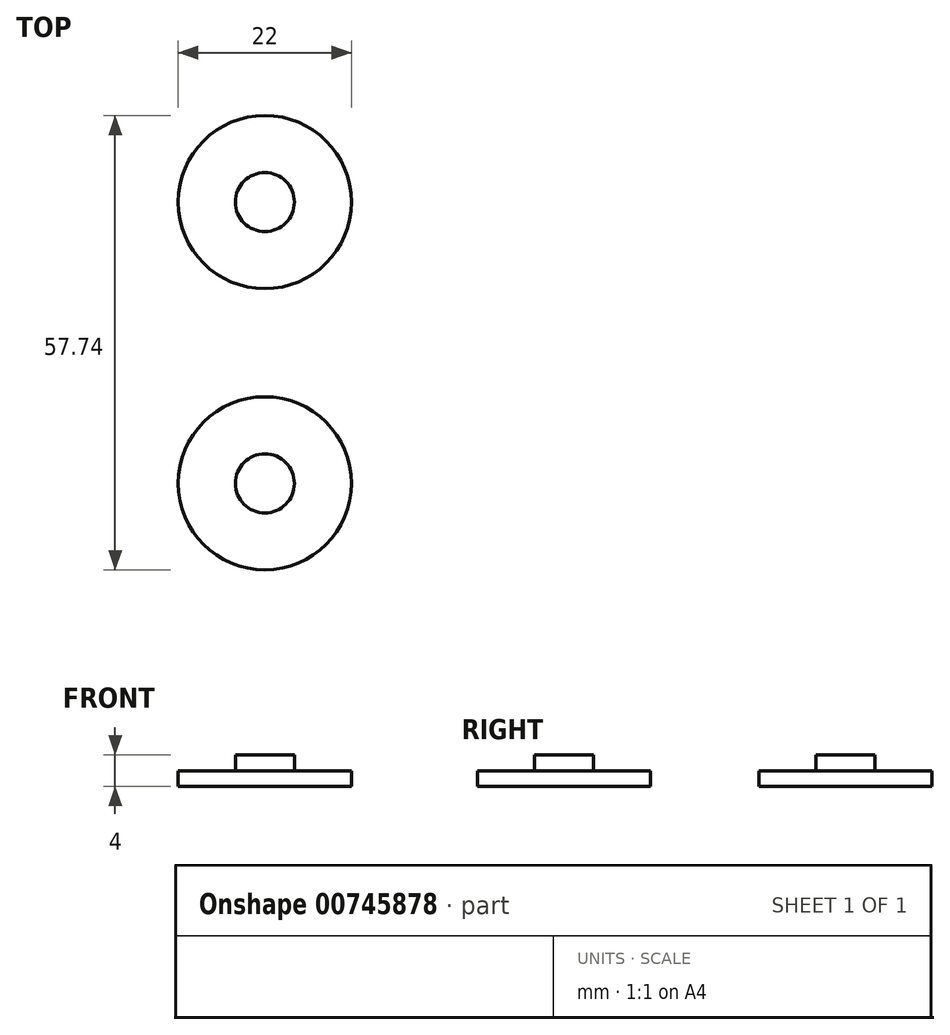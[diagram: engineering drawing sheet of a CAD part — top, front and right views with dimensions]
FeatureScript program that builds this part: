
annotation { "Feature Type Name" : "Feature", "Feature Type Description" : "" }
export const myFeature = defineFeature(function(context is Context, id is Id, definition is map)
    precondition{}
    {
        {
            var Q0;
            Q0=qCreatedBy(makeId("Top.planeOp"),FACE);
            var sketch = newSketch(context, id + "F0", { "sketchPlane" : qUnion([Q0])});
            skCircle(sketch, "E0", {"center": v(0, 0) * mm, "radius": 11 * mm});
            skLineSegment(sketch, "E1", {"start": v(0, 0) * mm, "end": v(0, 35.74) * mm, "construction": true});
            skCircle(sketch, "E2", {"center": v(0, 35.74) * mm, "radius": 11 * mm});
            skSolve(sketch);
        }
        {
            var Q0;
            Q0 = qSketchRegion(id + "F0", true);
            extrude(context, id + "F1", {"entities" : qUnion([Q0]), "depth" : 2 * mm, "offsetDistance" : 25 * mm});
        }
        {
            var Q0;
            Q0=makeQuery(id+"F1.opExtrude","CAP_FACE",FACE,{"disambiguationData":[OSD([sQuery(id+"F0.wireOp",EDGE,"E2")])],"isStart":false});
            var sketch = newSketch(context, id + "F2", { "sketchPlane" : qUnion([Q0])});
            skCircle(sketch, "E3.0", {"center": v(0, 35.74) * mm, "radius": 11 * mm});
            skCircle(sketch, "E4.0", {"center": v(0, 0) * mm, "radius": 11 * mm});
            skCircle(sketch, "E5", {"center": v(0, 35.74) * mm, "radius": 3.75 * mm});
            skCircle(sketch, "E6", {"center": v(0, 0) * mm, "radius": 3.75 * mm});
            skSolve(sketch);
        }
        {
            var Q0;
            Q0=makeQuery(id+"F2.imprint","IMPRINT",FACE,{"disambiguationData":[TD([[makeQuery(id+"F2.imprint","IMPRINT",EDGE,{"derivedFrom":sQuery(id+"F2.wireOp",EDGE,"E6")}),1.0]])]});
            var Q1;
            Q1=makeQuery(id+"F2.imprint","IMPRINT",FACE,{"disambiguationData":[TD([[makeQuery(id+"F2.imprint","IMPRINT",EDGE,{"derivedFrom":sQuery(id+"F2.wireOp",EDGE,"E5")}),1.0]])]});
            extrude(context, id + "F3", {"entities" : qUnion([Q0, Q1]), "operationType" : NewBodyOperationType.ADD, "depth" : 2 * mm, "offsetDistance" : 25 * mm});
        }
    });
